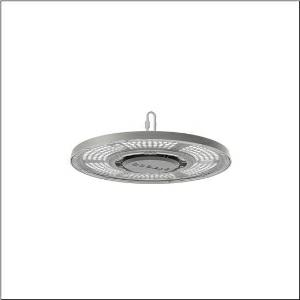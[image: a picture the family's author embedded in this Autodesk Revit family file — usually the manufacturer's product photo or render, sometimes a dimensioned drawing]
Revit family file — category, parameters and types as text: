
# Revit family: highbay_31-s_51hc417a4jmb
name_source: partatom
category: Lighting Fixtures
units: mm (PartAtom-declared; Revit-internal decimal feet)

## family parameters
Cut with Voids When Loaded = No
Host = Face
Light Source = No
Part Type = Normal
Room Calculation Point = No
Round Connector Dimension = Use Diameter
Shared = No

## types (1)
- Highbay 31-S (1 x LED, 20000 lm, 134 W, 4000K)
    Apparent Load = 134 VA
    CIE Flux Codes = 95 98 100 100 100
    Color Rendering = 80
    Color Temperature = 4000K
    Default Elevation = 1800 mm
    Description = Highbay 31-S, high bay luminaire, primary light control with lens, of PC, primary optical cover: cover panel, of PC, transparent, light emission: direct distribution, primary light characteristic: rotationally symmetric, installation type: suspended mounting, surface-mounted, LED, rated luminous flux: 20.000lm, luminous efficacy: 150lm/W, light colour: 840, colour temperature: 4000K, control gear: ON/OFF, with cable, 3x 1.0mm², free wire ends, mains connection: 220..240V, AC/DC, 0/50..60Hz, cable length: 1,5m, rated input power: 134W, housing, rotationally symmetric, of diecast aluminium, powder-coated, grey aluminium (RAL 9007), with hook on luminaire side, incl. screw, diameter: 339mm, protection rating (complete): IP65, insulation class (complete): insulation class I (protective earthing), certification: CE, ENEC, UKCA, protection symbol: D, impact resistance: IK08, permissible operating ambient temperature: -30..+45°C, standard: EN 60598-2-22, EN 60598, corresponds to IFS (International Featured Standards) requirements for safety and quality in the food industry, packaging unit: 1 piece
    Height = 141 mm
    Lamp = 1 x LED
    Lamp Light Flux = 20000 lm
    Lamp Power = 134 W
    Lamp count = 1
    Length = 339 mm
    Luminous efficacy = 149 lm/W
    Manufacturer = Siteco
    ModVariant = No
    Model = 51HC417A4JMB
    Mounting Place = Ceiling
    Mounting Type = Pendant
    Number of Poles = 1
    OnlyDefault = Yes
    Power Factor = 1
    Product Name = Highbay 31-S
    Product group = high bay luminaire
    ProductGroupID = 901
    Protection Class = Protection class I
    Protection Degree = IP 65
    RLX_Detail_Level = 1
    RLX_Emergency_Light_Flux = 0 lm
    RLX_Emergency_Type = 0
    RLX_Emergency_Type_DB = No
    RlxData = <blob elided: 106333 chars, md5=24ef51a2>
    Socket = socket
    Standby Power = 0 W
    System Light Flux = 20000 lm
    System Power = 134 W
    Type Comments = Product without accessories
    Type Image = l_1007237.jpg
    URL = http://relux.com
    VarID = ---
    Voltage = 0 V
    Weight = 0.00 kg
    Width = 0 mm  [stored 0 ft]

note: [stored X ft] marks values corroborated as IEEE doubles in the binary element streams (Revit-internal decimal feet)

## geometry (parser evidence)
native form markers: Blend x4, Sweep x10
no freeform markers — native parametric forms only
